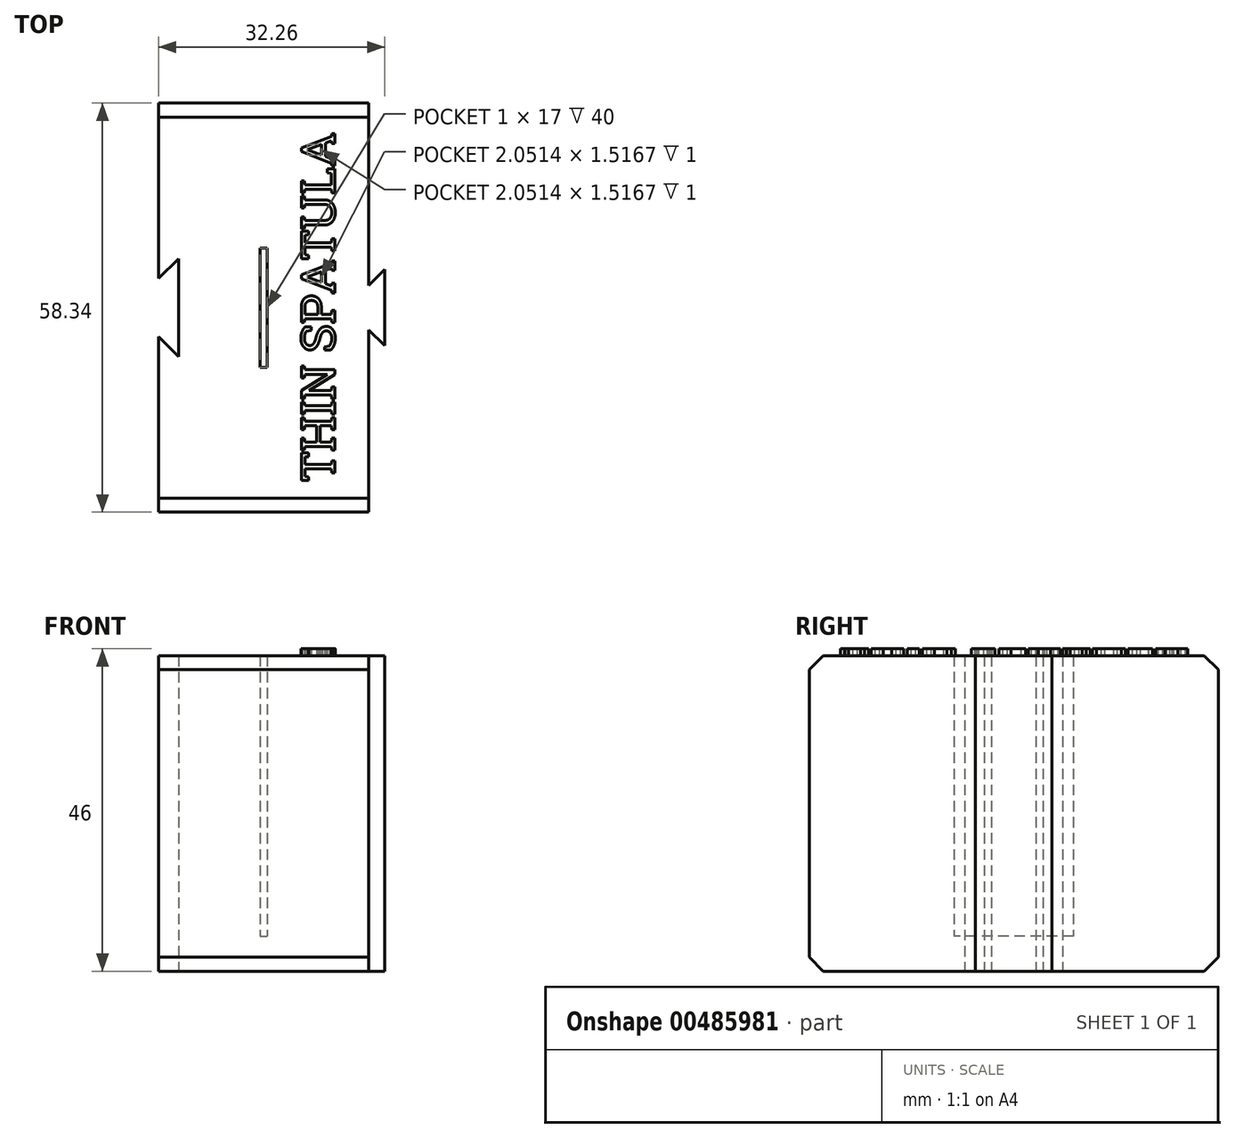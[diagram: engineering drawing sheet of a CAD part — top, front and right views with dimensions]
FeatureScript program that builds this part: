
annotation { "Feature Type Name" : "Feature", "Feature Type Description" : "" }
export const myFeature = defineFeature(function(context is Context, id is Id, definition is map)
    precondition{}
    {
        {
            var Q0;
            Q0=qCreatedBy(makeId("Top.planeOp"),FACE);
            var sketch = newSketch(context, id + "F0", { "sketchPlane" : qUnion([Q0])});
            skLineSegment(sketch, "E0", {"start": v(-15, 4.17) * mm, "end": v(-15, 29.17) * mm});
            skLineSegment(sketch, "E1", {"start": v(-15, 29.17) * mm, "end": v(15, 29.17) * mm});
            skLineSegment(sketch, "E2", {"start": v(15, 29.17) * mm, "end": v(15, 3.17) * mm});
            skLineSegment(sketch, "E3", {"start": v(-15, 4.17) * mm, "end": v(-12.17, 7) * mm});
            skLineSegment(sketch, "E4", {"start": v(-12.17, 7) * mm, "end": v(-12.17, 0) * mm});
            skLineSegment(sketch, "E5", {"start": v(15, 3.17) * mm, "end": v(17.26, 5.43) * mm});
            skLineSegment(sketch, "E6", {"start": v(17.26, 5.43) * mm, "end": v(17.26, -0.57) * mm});
            skLineSegment(sketch, "E7.MirrorCS", {"start": v(-15, -4.17) * mm, "end": v(-12.17, -7) * mm});
            skLineSegment(sketch, "E8.MirrorCS", {"start": v(15, -29.17) * mm, "end": v(15, -3.17) * mm});
            skLineSegment(sketch, "E9.MirrorCS", {"start": v(-12.17, -7) * mm, "end": v(-12.17, 0) * mm});
            skLineSegment(sketch, "E10.MirrorCS", {"start": v(-15, -4.17) * mm, "end": v(-15, -29.17) * mm});
            skLineSegment(sketch, "E11.MirrorCS", {"start": v(17.26, -5.43) * mm, "end": v(17.26, 0.57) * mm});
            skLineSegment(sketch, "E12.MirrorCS", {"start": v(15, -3.17) * mm, "end": v(17.26, -5.43) * mm});
            skLineSegment(sketch, "E13.MirrorCS", {"start": v(-15, -29.17) * mm, "end": v(15, -29.17) * mm});
            skLineSegment(sketch, "E14.bottom", {"start": v(-0.5, 8.5) * mm, "end": v(0.5, 8.5) * mm});
            skLineSegment(sketch, "E14.top", {"start": v(-0.5, -8.5) * mm, "end": v(0.5, -8.5) * mm});
            skLineSegment(sketch, "E14.left", {"start": v(-0.5, 8.5) * mm, "end": v(-0.5, -8.5) * mm});
            skLineSegment(sketch, "E14.right", {"start": v(0.5, 8.5) * mm, "end": v(0.5, -8.5) * mm});
            skPoint(sketch, "E14.middle", {"position": v(0, 0) * mm});
            skSolve(sketch);
        }
        {
            var Q0;
            Q0 = qSketchRegion(id + "F0", true);
            extrude(context, id + "F1", {"entities" : qUnion([Q0]), "depth" : 40 * mm});
        }
        {
            var Q0;
            Q0=makeQuery(id+"F0.imprint","IMPRINT",FACE,{"disambiguationData":[TD([[makeQuery(id+"F0.imprint","IMPRINT",EDGE,{"derivedFrom":sQuery(id+"F0.wireOp",EDGE,"E0")}),-1.0]])]});
            var Q1;
            Q1=makeQuery(id+"F0.imprint","IMPRINT",FACE,{"disambiguationData":[TD([[makeQuery(id+"F0.imprint","IMPRINT",EDGE,{"derivedFrom":sQuery(id+"F0.wireOp",EDGE,"E14.bottom")}),-1.0]])]});
            extrude(context, id + "F2", {"entities" : qUnion([Q0, Q1]), "operationType" : NewBodyOperationType.ADD, "oppositeDirection" : true, "depth" : 5 * mm});
        }
        {
            var Q0;
            Q0=makeQuery(id+"F2.opExtrude","CAP_EDGE",EDGE,{"disambiguationData":[OSD([sQuery(id+"F0.wireOp",EDGE,"E13.MirrorCS")])],"isStart":false});
            var Q1;
            Q1=makeQuery(id+"F2.opExtrude","CAP_EDGE",EDGE,{"disambiguationData":[OSD([sQuery(id+"F0.wireOp",EDGE,"E1")])],"isStart":false});
            var Q2;
            Q2=makeQuery(id+"F1.opExtrude","CAP_EDGE",EDGE,{"disambiguationData":[OSD([sQuery(id+"F0.wireOp",EDGE,"E13.MirrorCS")])],"isStart":false});
            var Q3;
            Q3=makeQuery(id+"F1.opExtrude","CAP_EDGE",EDGE,{"disambiguationData":[OSD([sQuery(id+"F0.wireOp",EDGE,"E1")])],"isStart":false});
            chamfer(context, id + "F3", {"entities" : qUnion([Q0, Q1, Q2, Q3]), "width" : 2 * mm, "tangentPropagation" : true});
        }
        {
            var Q0;
            Q0=makeQuery(id+"F1.opExtrude","CAP_FACE",FACE,{"disambiguationData":[OSD([sQuery(id+"F0.wireOp",EDGE,"E0"),sQuery(id+"F0.wireOp",EDGE,"E1"),sQuery(id+"F0.wireOp",EDGE,"E2"),sQuery(id+"F0.wireOp",EDGE,"E3"),sQuery(id+"F0.wireOp",EDGE,"E4"),sQuery(id+"F0.wireOp",EDGE,"E5"),sQuery(id+"F0.wireOp",EDGE,"E6"),sQuery(id+"F0.wireOp",EDGE,"E7.MirrorCS"),sQuery(id+"F0.wireOp",EDGE,"E8.MirrorCS"),sQuery(id+"F0.wireOp",EDGE,"E9.MirrorCS"),sQuery(id+"F0.wireOp",EDGE,"E10.MirrorCS"),sQuery(id+"F0.wireOp",EDGE,"E11.MirrorCS"),sQuery(id+"F0.wireOp",EDGE,"E12.MirrorCS"),sQuery(id+"F0.wireOp",EDGE,"E13.MirrorCS"),sQuery(id+"F0.wireOp",EDGE,"E14.bottom"),sQuery(id+"F0.wireOp",EDGE,"E14.top"),sQuery(id+"F0.wireOp",EDGE,"E14.left"),sQuery(id+"F0.wireOp",EDGE,"E14.right")])],"isStart":false});
            var sketch = newSketch(context, id + "F4", { "sketchPlane" : qUnion([Q0])});
            skText(sketch, "E15", { "text": "THIN SPATULA", "fontName": "RobotoSlab-Regular.ttf"});
            const initialGuessF4  = {"E15": [0.01014, -0.0248, 0, 1, 0.00484]};
            skSetInitialGuess(sketch, initialGuessF4);
            skSolve(sketch);
        }
        {
            var Q0;
            Q0 = qSketchRegion(id + "F4", true);
            extrude(context, id + "F5", {"entities" : qUnion([Q0]), "operationType" : NewBodyOperationType.ADD, "depth" : 1 * mm});
        }
    });
